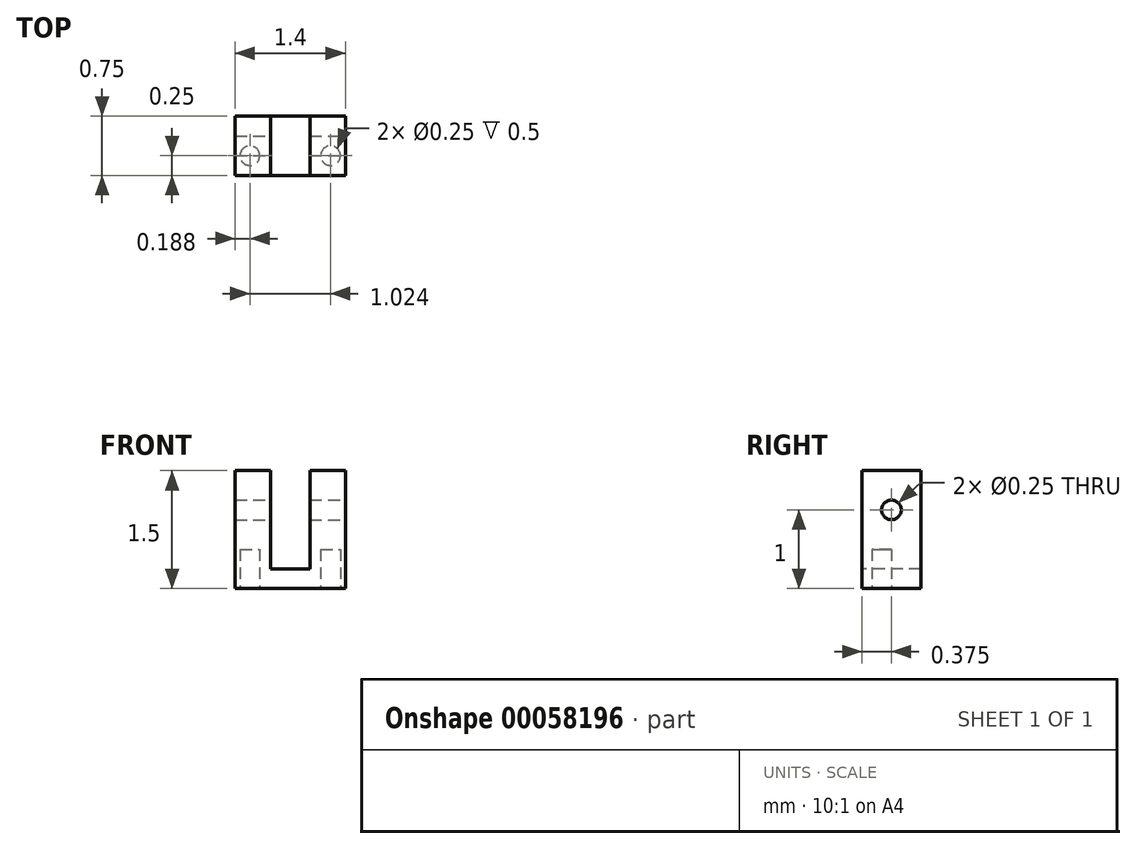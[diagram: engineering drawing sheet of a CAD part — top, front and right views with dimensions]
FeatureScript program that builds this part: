
annotation { "Feature Type Name" : "Feature", "Feature Type Description" : "" }
export const myFeature = defineFeature(function(context is Context, id is Id, definition is map)
    precondition{}
    {
        {
            var Q0;
            Q0=qCreatedBy(makeId("Front.planeOp"),FACE);
            var sketch = newSketch(context, id + "F0", { "sketchPlane" : qUnion([Q0])});
            skLineSegment(sketch, "E0.rect.bottom", {"start": v(0.7, -0.75) * mm, "end": v(-0.7, -0.75) * mm});
            skLineSegment(sketch, "E0.rect.top", {"start": v(0.7, 0.75) * mm, "end": v(-0.7, 0.75) * mm});
            skLineSegment(sketch, "E0.rect.left", {"start": v(0.7, -0.75) * mm, "end": v(0.7, 0.75) * mm});
            skLineSegment(sketch, "E0.rect.right", {"start": v(-0.7, -0.75) * mm, "end": v(-0.7, 0.75) * mm});
            skPoint(sketch, "E0.rect.middle", {"position": v(0, 0) * mm});
            skSolve(sketch);
        }
        {
            var Q0;
            Q0 = qSketchRegion(id + "F0", true);
            extrude(context, id + "F1", {"entities" : qUnion([Q0]), "depth" : 0.75 * mm});
        }
        {
            var Q0;
            Q0=qCreatedBy(makeId("Right.planeOp"),FACE);
            var sketch = newSketch(context, id + "F2", { "sketchPlane" : qUnion([Q0])});
            skCircle(sketch, "E1", {"center": v(-0.38, 0.25) * mm, "radius": 0.12 * mm});
            skSolve(sketch);
        }
        {
            var Q0;
            Q0 = qSketchRegion(id + "F2", true);
            var Q1;
            Q1 = qSketchRegion(id + "F4", true);
            extrude(context, id + "F3", {"entities" : qUnion([Q0, Q1]), "operationType" : NewBodyOperationType.REMOVE, "endBound" : BoundingType.SYMMETRIC, "oppositeDirection" : true, "depth" : 25 * mm});
        }
        {
            var Q0;
            Q0=makeQuery(id+"F1.opExtrude","SWEPT_FACE",FACE,{"disambiguationData":[OSD([sQuery(id+"F0.wireOp",EDGE,"E0.rect.bottom")])]});
            var sketch = newSketch(context, id + "F4", { "sketchPlane" : qUnion([Q0])});
            skCircle(sketch, "E2", {"center": v(0.51, 0.5) * mm, "radius": 0.12 * mm});
            skCircle(sketch, "E3", {"center": v(-0.51, 0.5) * mm, "radius": 0.12 * mm});
            skSolve(sketch);
        }
        {
            var Q0;
            Q0 = qSketchRegion(id + "F4", true);
            extrude(context, id + "F5", {"entities" : qUnion([Q0]), "operationType" : NewBodyOperationType.REMOVE, "oppositeDirection" : true, "depth" : 0.5 * mm});
        }
        {
            var Q0;
            Q0=makeQuery(id+"F1.opExtrude","CAP_FACE",FACE,{"disambiguationData":[OSD([sQuery(id+"F0.wireOp",EDGE,"E0.rect.bottom"),sQuery(id+"F0.wireOp",EDGE,"E0.rect.top"),sQuery(id+"F0.wireOp",EDGE,"E0.rect.left"),sQuery(id+"F0.wireOp",EDGE,"E0.rect.right")])],"isStart":false});
            var sketch = newSketch(context, id + "F6", { "sketchPlane" : qUnion([Q0])});
            skLineSegment(sketch, "E4", {"start": v(-0.7, 0.75) * mm, "end": v(-0.25, 0.75) * mm});
            skLineSegment(sketch, "E5", {"start": v(0.7, -0.75) * mm, "end": v(0.7, -0.5) * mm});
            skLineSegment(sketch, "E6", {"start": v(-0.25, -0.5) * mm, "end": v(0.25, -0.5) * mm});
            skLineSegment(sketch, "E7", {"start": v(-0.25, 0.75) * mm, "end": v(-0.25, -0.5) * mm});
            skLineSegment(sketch, "E8", {"start": v(0.25, -0.5) * mm, "end": v(0.25, 0.75) * mm});
            skSolve(sketch);
        }
        {
            var Q0;
            Q0 = qSketchRegion(id + "F6", true);
            var Q1;
            Q1=makeQuery(id+"F6.imprint","IMPRINT",FACE,{"disambiguationData":[TD([[makeQuery(id+"F6.imprint","IMPRINT",EDGE,{"derivedFrom":sQuery(id+"F6.wireOp",EDGE,"E6")}),1.0]])]});
            extrude(context, id + "F7", {"entities" : qUnion([Q0, Q1]), "operationType" : NewBodyOperationType.REMOVE, "oppositeDirection" : true, "depth" : 25 * mm});
        }
    });
